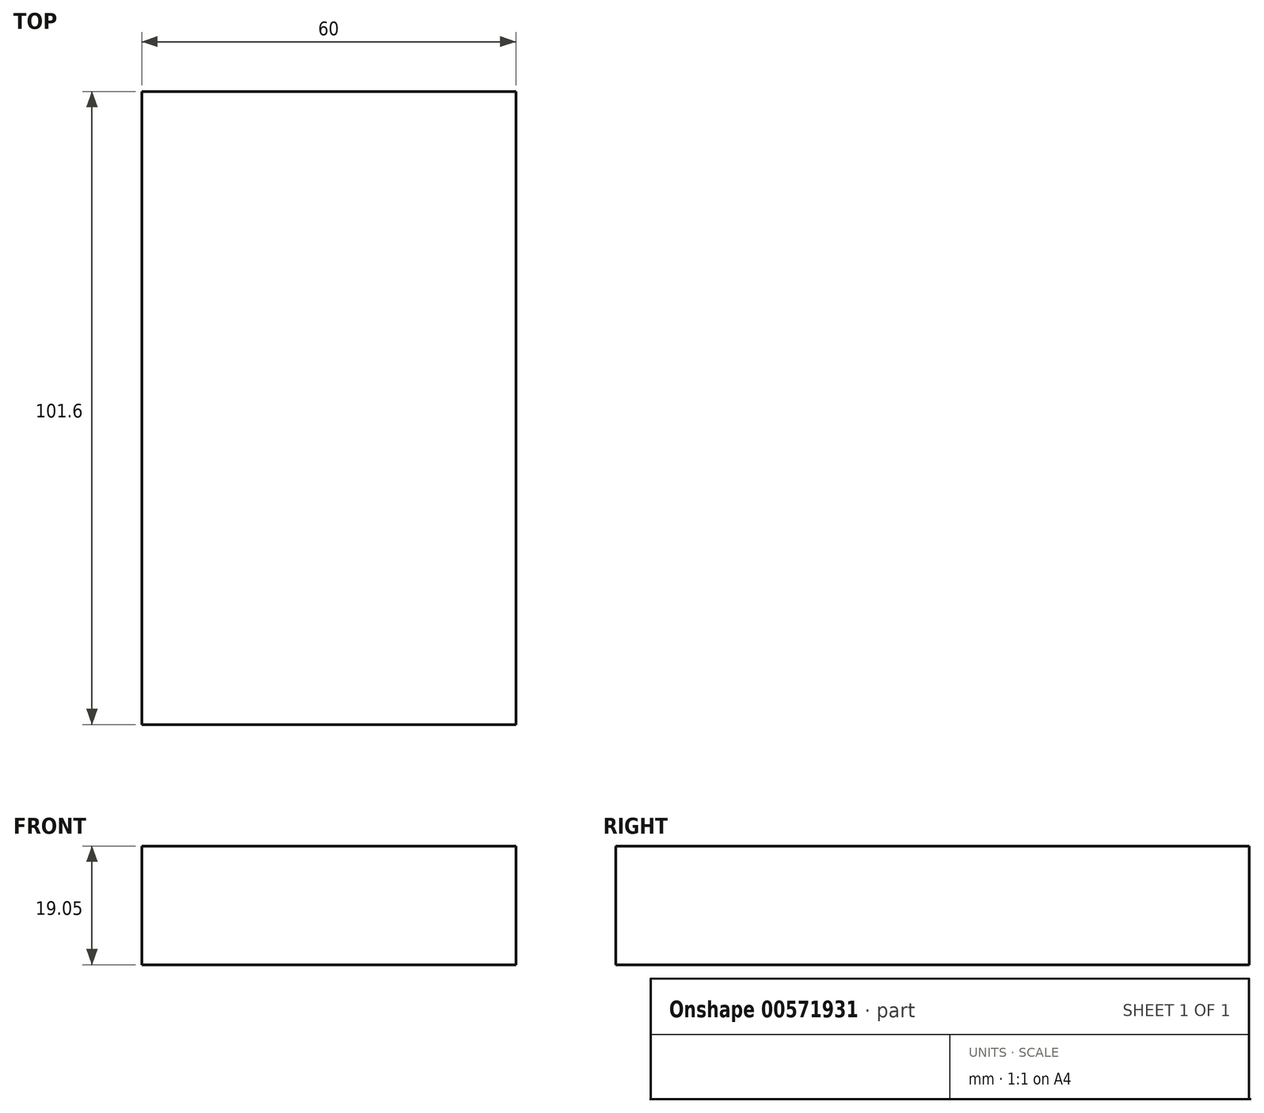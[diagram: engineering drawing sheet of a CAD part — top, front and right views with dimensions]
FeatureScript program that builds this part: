
annotation { "Feature Type Name" : "Feature", "Feature Type Description" : "" }
export const myFeature = defineFeature(function(context is Context, id is Id, definition is map)
    precondition{}
    {
        {
            var Q0;
            Q0=qCreatedBy(makeId("Top.planeOp"),FACE);
            var sketch = newSketch(context, id + "F0", { "sketchPlane" : qUnion([Q0])});
            skLineSegment(sketch, "E0", {"start": v(-87, -113.5) * mm, "end": v(-27, -113.5) * mm});
            skLineSegment(sketch, "E1", {"start": v(-27, -113.5) * mm, "end": v(-27, -11.9) * mm});
            skLineSegment(sketch, "E2", {"start": v(-27, -11.9) * mm, "end": v(-87, -11.9) * mm});
            skLineSegment(sketch, "E3", {"start": v(-87, -11.9) * mm, "end": v(-87, -113.5) * mm});
            skSolve(sketch);
        }
        {
            var Q0;
            Q0 = qSketchRegion(id + "F0", true);
            extrude(context, id + "F1", {"entities" : qUnion([Q0]), "depth" : 19.05 * mm, "offsetDistance" : 25.4 * mm});
        }
    });
